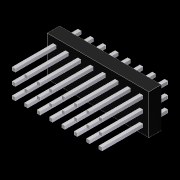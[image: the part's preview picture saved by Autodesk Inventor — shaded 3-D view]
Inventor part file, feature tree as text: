
AUTODESK INVENTOR PART (.ipt)
format: ipt  version: 2012 (Build 160160000, 160)  size: 211,968 bytes
history: native  units: in
note: dims shown in document units (in); Inventor stores cm internally (conversion verified against a paired STEP export)
features: extrude x3, sketch x1, pattern_linear x1
ambient origin geometry x8: Origin, YZ Plane, XZ Plane, XY Plane, X Axis, Y Axis, Z Axis, Center Point
bodies: Solid1 (feature_tree)
feature tree (5):
  sketch  "Sketch1"  dims[d0=0.1in d1=0.0in d2=0.33in d3=0.0in d4=0.2in d5=0.0in d6=1.1811in d8=0.1in d9=3.1496in d11=0.1in]
  extrude  "Extrusion1"  Depth=0.33in TaperAngle=0.0deg
  extrude  "Extrusion2"  Depth=0.2in TaperAngle=0.0deg
  extrude  "Extrusion3"  Depth=1.1811in
  pattern_linear  "Rectangular Pattern1"  Count1=8 Spacing1=0.1in
